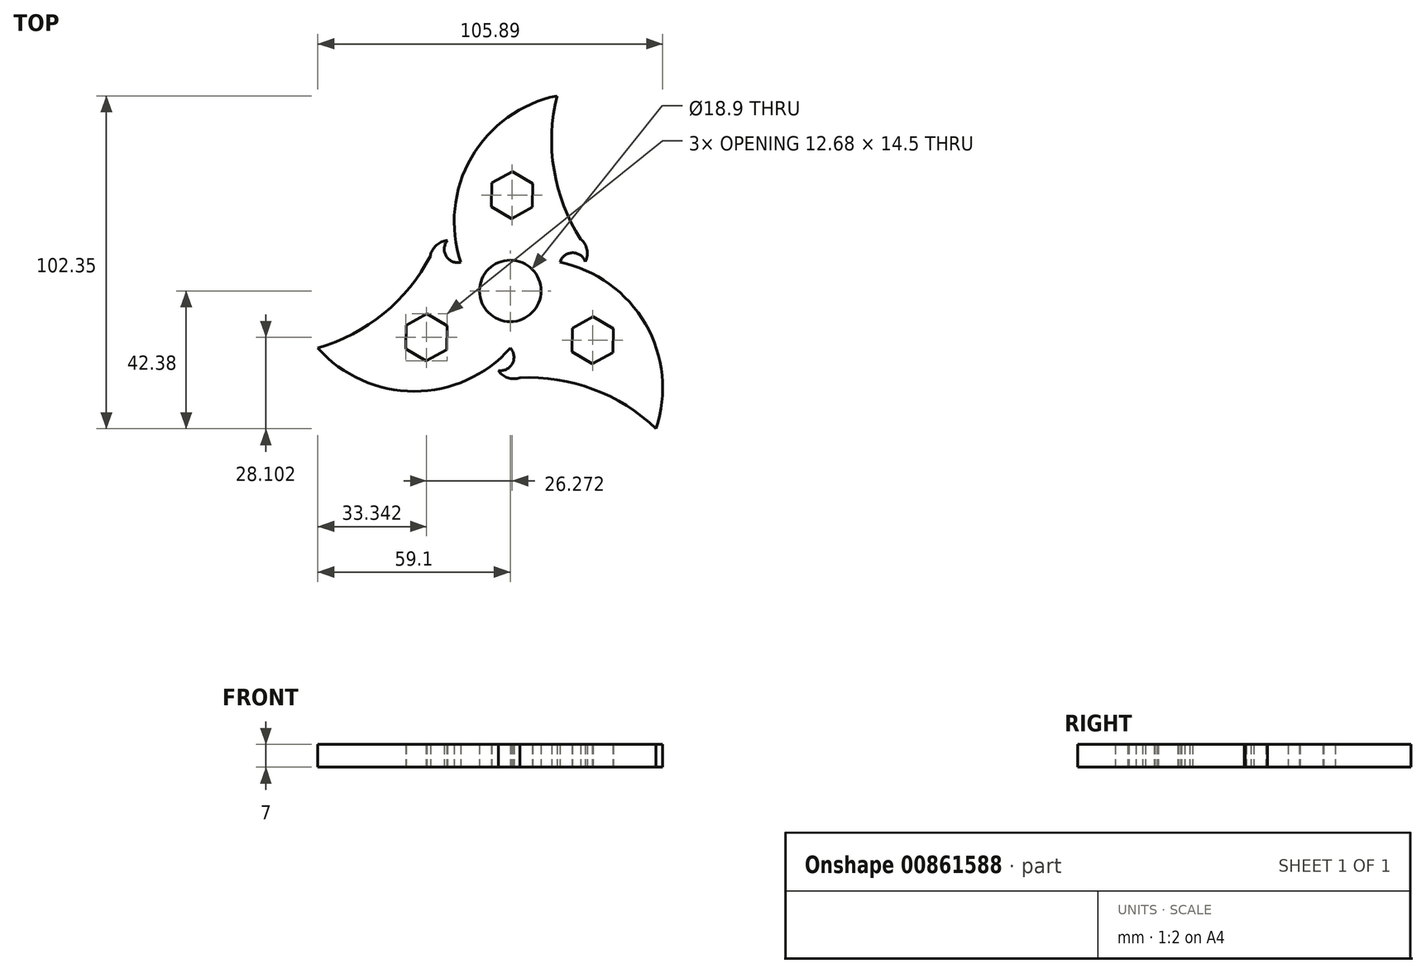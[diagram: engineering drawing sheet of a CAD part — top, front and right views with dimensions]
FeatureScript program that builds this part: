
annotation { "Feature Type Name" : "Feature", "Feature Type Description" : "" }
export const myFeature = defineFeature(function(context is Context, id is Id, definition is map)
    precondition{}
    {
        {
            var Q0;
            Q0=qCreatedBy(makeId("Top.planeOp"),FACE);
            var sketch = newSketch(context, id + "F0", { "sketchPlane" : qUnion([Q0])});
            skCircle(sketch, "E0", {"center": v(0, 0) * mm, "radius": 9.45 * mm});
            skArc(sketch, "E1", {"start": v(-59.1, -17.59) * mm, "mid": v(-38.9, -6.96) * mm, "end": v(-24.56, 10.8) * mm});
            skArc(sketch, "E2", {"start": v(-59.1, -17.59) * mm, "mid": v(-29.55, -30.86) * mm, "end": v(0, -17.59) * mm});
            skArc(sketch, "E3.1.0", {"start": v(44.78, -42.38) * mm, "mid": v(25.47, -30.2) * mm, "end": v(2.92, -26.67) * mm});
            skArc(sketch, "E3.1.1", {"start": v(44.78, -42.38) * mm, "mid": v(41.5, -10.16) * mm, "end": v(15.23, 8.8) * mm});
            skArc(sketch, "E3.2.0", {"start": v(14.32, 59.97) * mm, "mid": v(13.42, 37.16) * mm, "end": v(21.64, 15.86) * mm});
            skArc(sketch, "E3.2.1", {"start": v(14.32, 59.97) * mm, "mid": v(-11.95, 41.02) * mm, "end": v(-15.23, 8.8) * mm});
            skArc(sketch, "E4", {"start": v(-19.33, 15.45) * mm, "mid": v(-22.74, 14.03) * mm, "end": v(-24.56, 10.8) * mm});
            skArc(sketch, "E5", {"start": v(-19.33, 15.45) * mm, "mid": v(-19.68, 10.65) * mm, "end": v(-15.23, 8.8) * mm});
            skArc(sketch, "E6.1.0", {"start": v(-3.72, -24.47) * mm, "mid": v(-0.78, -26.71) * mm, "end": v(2.92, -26.67) * mm});
            skArc(sketch, "E6.1.1", {"start": v(-3.72, -24.47) * mm, "mid": v(0.62, -22.37) * mm, "end": v(0, -17.59) * mm});
            skArc(sketch, "E6.2.0", {"start": v(23.05, 9.01) * mm, "mid": v(23.52, 12.68) * mm, "end": v(21.64, 15.86) * mm});
            skArc(sketch, "E6.2.1", {"start": v(23.05, 9.01) * mm, "mid": v(19.06, 11.72) * mm, "end": v(15.23, 8.8) * mm});
            skLineSegment(sketch, "E7", {"start": v(0, 0) * mm, "end": v(1.07, 61.45) * mm, "construction": true});
            skCircle(sketch, "E8.cCircle", {"center": v(0.51, 29.45) * mm, "radius": 7.25 * mm, "construction": true});
            skLineSegment(sketch, "E8.0", {"start": v(0.64, 36.7) * mm, "end": v(6.85, 32.96) * mm});
            skLineSegment(sketch, "E8.1", {"start": v(6.85, 32.96) * mm, "end": v(6.73, 25.71) * mm});
            skLineSegment(sketch, "E8.2", {"start": v(6.73, 25.71) * mm, "end": v(0.39, 22.2) * mm});
            skLineSegment(sketch, "E8.3", {"start": v(0.39, 22.2) * mm, "end": v(-5.83, 25.93) * mm});
            skLineSegment(sketch, "E8.4", {"start": v(-5.83, 25.93) * mm, "end": v(-5.7, 33.18) * mm});
            skLineSegment(sketch, "E8.5", {"start": v(-5.7, 33.18) * mm, "end": v(0.64, 36.7) * mm});
            skLineSegment(sketch, "E9.1.0", {"start": v(-32.1, -17.8) * mm, "end": v(-31.97, -10.54) * mm});
            skLineSegment(sketch, "E9.1.1", {"start": v(-31.97, -10.54) * mm, "end": v(-25.63, -7.03) * mm});
            skLineSegment(sketch, "E9.1.2", {"start": v(-25.63, -7.03) * mm, "end": v(-19.42, -10.76) * mm});
            skLineSegment(sketch, "E9.1.3", {"start": v(-19.42, -10.76) * mm, "end": v(-19.54, -18.01) * mm});
            skLineSegment(sketch, "E9.1.4", {"start": v(-19.54, -18.01) * mm, "end": v(-25.88, -21.53) * mm});
            skLineSegment(sketch, "E9.1.5", {"start": v(-25.88, -21.53) * mm, "end": v(-32.1, -17.8) * mm});
            skLineSegment(sketch, "E9.2.0", {"start": v(31.46, -18.9) * mm, "end": v(25.12, -22.42) * mm});
            skLineSegment(sketch, "E9.2.1", {"start": v(25.12, -22.42) * mm, "end": v(18.9, -18.68) * mm});
            skLineSegment(sketch, "E9.2.2", {"start": v(18.9, -18.68) * mm, "end": v(19.03, -11.43) * mm});
            skLineSegment(sketch, "E9.2.3", {"start": v(19.03, -11.43) * mm, "end": v(25.37, -7.92) * mm});
            skLineSegment(sketch, "E9.2.4", {"start": v(25.37, -7.92) * mm, "end": v(31.58, -11.65) * mm});
            skLineSegment(sketch, "E9.2.5", {"start": v(31.58, -11.65) * mm, "end": v(31.46, -18.9) * mm});
            skSolve(sketch);
        }
        {
            var Q0;
            Q0=makeQuery(id+"F0.imprint","IMPRINT",FACE,{"disambiguationData":[TD([[makeQuery(id+"F0.imprint","IMPRINT",EDGE,{"derivedFrom":sQuery(id+"F0.wireOp",EDGE,"E0")}),-1.0]])]});
            extrude(context, id + "F1", {"entities" : qUnion([Q0]), "depth" : 7 * mm, "offsetDistance" : 25 * mm});
        }
    });
